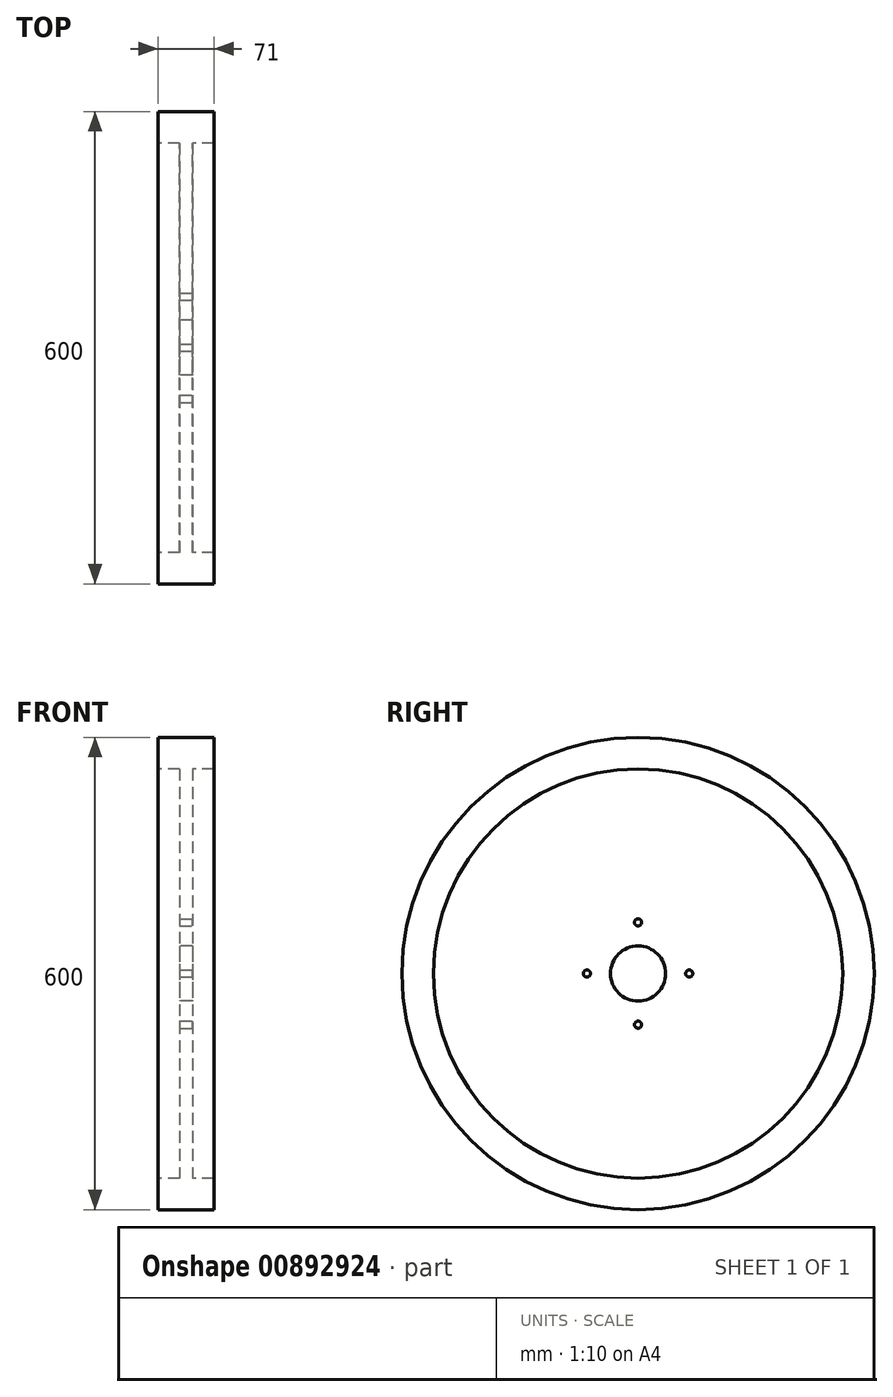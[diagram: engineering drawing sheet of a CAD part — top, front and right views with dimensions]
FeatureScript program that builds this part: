
annotation { "Feature Type Name" : "Feature", "Feature Type Description" : "" }
export const myFeature = defineFeature(function(context is Context, id is Id, definition is map)
    precondition{}
    {
        {
            var Q0;
            Q0=qCreatedBy(makeId("Front.planeOp"),FACE);
            var sketch = newSketch(context, id + "F0", { "sketchPlane" : qUnion([Q0])});
            skLineSegment(sketch, "E0", {"start": v(0, 35) * mm, "end": v(8, 35) * mm});
            skLineSegment(sketch, "E1", {"start": v(8, 35) * mm, "end": v(8, 260) * mm});
            skLineSegment(sketch, "E2", {"start": v(8, 260) * mm, "end": v(35.5, 260) * mm});
            skLineSegment(sketch, "E3", {"start": v(35.5, 260) * mm, "end": v(35.5, 300) * mm});
            skLineSegment(sketch, "E4", {"start": v(35.5, 300) * mm, "end": v(0, 300) * mm});
            skLineSegment(sketch, "E5.MirrorCS", {"start": v(0, 35) * mm, "end": v(-8, 35) * mm});
            skLineSegment(sketch, "E6.MirrorCS", {"start": v(-35.5, 300) * mm, "end": v(0, 300) * mm});
            skLineSegment(sketch, "E7.MirrorCS", {"start": v(-8, 260) * mm, "end": v(-35.5, 260) * mm});
            skLineSegment(sketch, "E8.MirrorCS", {"start": v(-8, 35) * mm, "end": v(-8, 260) * mm});
            skLineSegment(sketch, "E9.MirrorCS", {"start": v(-35.5, 260) * mm, "end": v(-35.5, 300) * mm});
            skLineSegment(sketch, "E10", {"start": v(0, 0) * mm, "end": v(113.88, 0) * mm, "construction": true});
            skSolve(sketch);
        }
        {
            var Q0;
            Q0 = qSketchRegion(id + "F0", true);
            var Q1;
            Q1=sQuery(id+"F0.wireOp",EDGE,"E10");
            revolve(context, id + "F1", {"surfaceOperationType" : NewSurfaceOperationType.NEW, "entities" : qUnion([Q0]), "axis" : qUnion([Q1]), "revolveType" : RevolveType.FULL});
        }
        {
            var Q0;
            Q0=makeQuery(id+"F1.opRevolve","SWEPT_FACE",FACE,{"disambiguationData":[OSD([sQuery(id+"F0.wireOp",EDGE,"E1")])]});
            var sketch = newSketch(context, id + "F2", { "sketchPlane" : qUnion([Q0])});
            skCircle(sketch, "E11", {"center": v(0, 65) * mm, "radius": 4.5 * mm});
            skCircle(sketch, "E12.1.0", {"center": v(-65, 0) * mm, "radius": 4.5 * mm});
            skCircle(sketch, "E12.2.0", {"center": v(0, -65) * mm, "radius": 4.5 * mm});
            skCircle(sketch, "E12.3.0", {"center": v(65, 0) * mm, "radius": 4.5 * mm});
            skPoint(sketch, "E12.center", {"position": v(0, 0) * mm});
            skSolve(sketch);
        }
        {
            var Q0;
            Q0 = qSketchRegion(id + "F2", true);
            extrude(context, id + "F3", {"entities" : qUnion([Q0]), "operationType" : NewBodyOperationType.REMOVE, "oppositeDirection" : true, "depth" : 25 * mm, "offsetDistance" : 25 * mm});
        }
    });
